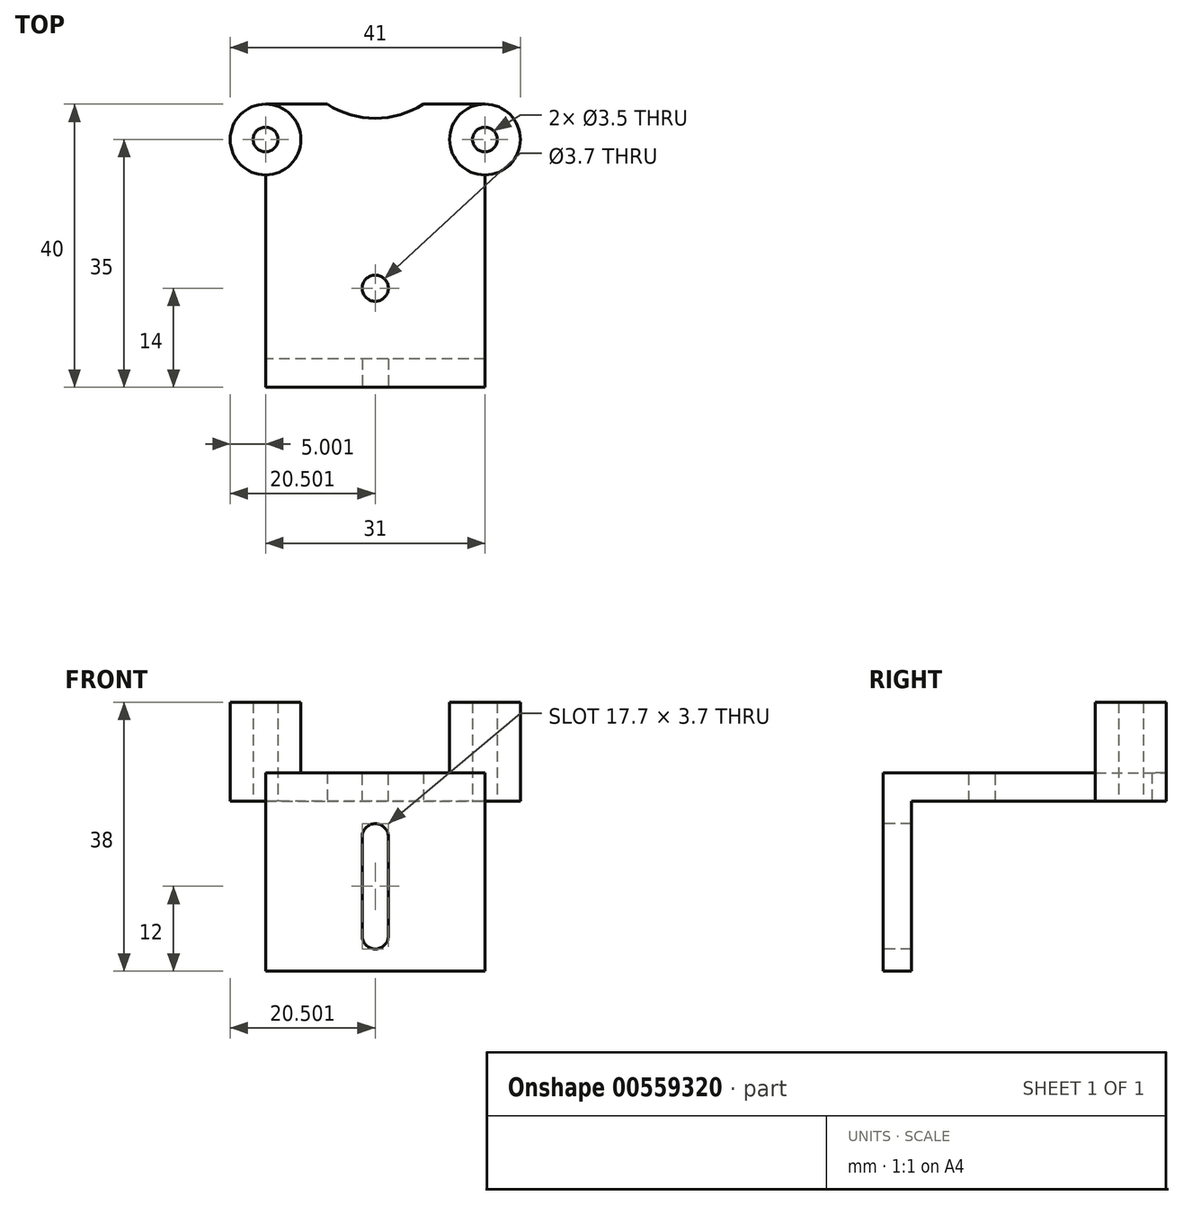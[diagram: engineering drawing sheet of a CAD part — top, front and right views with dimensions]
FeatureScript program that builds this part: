
annotation { "Feature Type Name" : "Feature", "Feature Type Description" : "" }
export const myFeature = defineFeature(function(context is Context, id is Id, definition is map)
    precondition{}
    {
        {
            var Q0;
            Q0=qCreatedBy(makeId("Top.planeOp"),FACE);
            var sketch = newSketch(context, id + "F0", { "sketchPlane" : qUnion([Q0])});
            skLineSegment(sketch, "E0", {"start": v(-4.15, -31) * mm, "end": v(26.85, -31) * mm});
            skCircle(sketch, "E1", {"center": v(26.85, -31) * mm, "radius": 1.75 * mm});
            skCircle(sketch, "E2", {"center": v(-4.15, -31) * mm, "radius": 1.75 * mm});
            skCircle(sketch, "E3", {"center": v(-4.15, -31) * mm, "radius": 5 * mm});
            skCircle(sketch, "E4", {"center": v(26.85, -31) * mm, "radius": 5 * mm});
            skLineSegment(sketch, "E5", {"start": v(-4.15, -31) * mm, "end": v(-4.15, -26) * mm, "construction": true});
            skLineSegment(sketch, "E6", {"start": v(-4.15, -26) * mm, "end": v(26.85, -26) * mm});
            skLineSegment(sketch, "E7", {"start": v(26.85, -26) * mm, "end": v(26.85, -36) * mm, "construction": true});
            skLineSegment(sketch, "E8", {"start": v(26.85, -36) * mm, "end": v(-4.15, -36) * mm});
            skLineSegment(sketch, "E9", {"start": v(-4.15, -36) * mm, "end": v(-4.15, -31) * mm, "construction": true});
            skLineSegment(sketch, "E10", {"start": v(26.85, -31) * mm, "end": v(26.85, 0) * mm});
            skLineSegment(sketch, "E11", {"start": v(26.85, 0) * mm, "end": v(-4.15, 0) * mm});
            skLineSegment(sketch, "E12", {"start": v(-4.15, 0) * mm, "end": v(-4.15, -31) * mm});
            skLineSegment(sketch, "E13", {"start": v(-4.15, -31) * mm, "end": v(26.85, 0) * mm, "construction": true});
            skLineSegment(sketch, "E14", {"start": v(-4.15, 0) * mm, "end": v(26.85, -31) * mm, "construction": true});
            skCircle(sketch, "E15", {"center": v(11.35, -15.5) * mm, "radius": 12.5 * mm});
            skSolve(sketch);
        }
        {
            var Q0;
            Q0=makeQuery(id+"F0.imprint","IMPRINT",FACE,{"disambiguationData":[TD([[makeQuery(id+"F0.imprint","IMPRINT",EDGE,{"derivedFrom":sQuery(id+"F0.wireOp",EDGE,"E2")}),-1.0]])]});
            var Q1;
            {var subQ5=sQuery(id+"F0.wireOp",EDGE,"E6");Q1=makeQuery(id+"F0.imprint","IMPRINT",FACE,{"disambiguationData":[TD([[makeQuery(id+"F0.imprint","IMPRINT",EDGE,{"derivedFrom":subQ5}),-1.0]])]});}
            var Q2;
            Q2=makeQuery(id+"F0.imprint","IMPRINT",FACE,{"disambiguationData":[TD([[makeQuery(id+"F0.imprint","IMPRINT",EDGE,{"derivedFrom":sQuery(id+"F0.wireOp",EDGE,"E1")}),-1.0]])]});
            var Q3;
            {var subQ5=sQuery(id+"F0.wireOp",EDGE,"E8");Q3=makeQuery(id+"F0.imprint","IMPRINT",FACE,{"disambiguationData":[TD([[makeQuery(id+"F0.imprint","IMPRINT",EDGE,{"derivedFrom":subQ5}),-1.0]])]});}
            var Q4;
            {var subQ1=sQuery(id+"F0.wireOp",EDGE,"E4");var subQ4=sQuery(id+"F0.wireOp",EDGE,"E0");var subQ5=makeQuery(id+"F0.imprint","INTERSECT",VERTEX,{"derivedFrom":[subQ4,subQ1]});Q4=makeQuery(id+"F0.imprint","IMPRINT",FACE,{"disambiguationData":[TD([[makeQuery(id+"F0.imprint","IMPRINT",EDGE,{"disambiguationData":[TD([[subQ5,-1.0]])],"derivedFrom":subQ4}),-1.0]])]});}
            var Q5;
            {var subQ4=sQuery(id+"F0.wireOp",EDGE,"E2");var subQ5=sQuery(id+"F0.wireOp",EDGE,"E0");var subQ6=makeQuery(id+"F0.imprint","INTERSECT",VERTEX,{"derivedFrom":[subQ5,subQ4]});Q5=makeQuery(id+"F0.imprint","IMPRINT",FACE,{"disambiguationData":[TD([[makeQuery(id+"F0.imprint","IMPRINT",EDGE,{"disambiguationData":[TD([[subQ6,-1.0]])],"derivedFrom":subQ5}),-1.0]])]});}
            extrude(context, id + "F1", {"entities" : qUnion([Q0, Q1, Q2, Q3, Q4, Q5]), "depth" : 4 * mm, "offsetDistance" : 25 * mm});
        }
        {
            var Q0;
            Q0=makeQuery(id+"F0.imprint","IMPRINT",FACE,{"disambiguationData":[TD([[makeQuery(id+"F0.imprint","IMPRINT",EDGE,{"derivedFrom":sQuery(id+"F0.wireOp",EDGE,"E2")}),-1.0]])]});
            var Q1;
            Q1=makeQuery(id+"F0.imprint","IMPRINT",FACE,{"disambiguationData":[TD([[makeQuery(id+"F0.imprint","IMPRINT",EDGE,{"derivedFrom":sQuery(id+"F0.wireOp",EDGE,"E1")}),-1.0]])]});
            var Q2;
            {var subQ4=sQuery(id+"F0.wireOp",EDGE,"E2");var subQ5=sQuery(id+"F0.wireOp",EDGE,"E0");var subQ6=makeQuery(id+"F0.imprint","INTERSECT",VERTEX,{"derivedFrom":[subQ5,subQ4]});Q2=makeQuery(id+"F0.imprint","IMPRINT",FACE,{"disambiguationData":[TD([[makeQuery(id+"F0.imprint","IMPRINT",EDGE,{"disambiguationData":[TD([[subQ6,-1.0]])],"derivedFrom":subQ5}),-1.0]])]});}
            var Q3;
            {var subQ1=sQuery(id+"F0.wireOp",EDGE,"E4");var subQ4=sQuery(id+"F0.wireOp",EDGE,"E0");var subQ5=makeQuery(id+"F0.imprint","INTERSECT",VERTEX,{"derivedFrom":[subQ4,subQ1]});Q3=makeQuery(id+"F0.imprint","IMPRINT",FACE,{"disambiguationData":[TD([[makeQuery(id+"F0.imprint","IMPRINT",EDGE,{"disambiguationData":[TD([[subQ5,-1.0]])],"derivedFrom":subQ4}),-1.0]])]});}
            extrude(context, id + "F2", {"entities" : qUnion([Q0, Q1, Q2, Q3]), "operationType" : NewBodyOperationType.ADD, "depth" : 14 * mm, "offsetDistance" : 25 * mm});
        }
        {
            var Q0;
            Q0=makeQuery(id+"F1.opExtrude","SWEPT_FACE",FACE,{"disambiguationData":[OSD([sQuery(id+"F0.wireOp",EDGE,"E8")])]});
            extrude(context, id + "F3", {"entities" : qUnion([Q0]), "operationType" : NewBodyOperationType.ADD, "depth" : 30 * mm, "offsetDistance" : 25 * mm});
        }
        {
            var Q0;
            {var subQ0=sQuery(id+"F0.wireOp",EDGE,"E8");Q0=makeQuery(id+"F3.boolean.opBoolean","MERGE",FACE,{"derivedFrom":[makeQuery(id+"F1.opExtrude","CAP_FACE",FACE,{"disambiguationData":[OSD([sQuery(id+"F0.wireOp",EDGE,"E1"),sQuery(id+"F0.wireOp",EDGE,"E2"),sQuery(id+"F0.wireOp",EDGE,"E3"),sQuery(id+"F0.wireOp",EDGE,"E4"),sQuery(id+"F0.wireOp",EDGE,"E6"),subQ0])],"isStart":true}),makeQuery(id+"F3.opExtrude","SWEPT_FACE",FACE,{"disambiguationData":[OSD([subQ0]),TDD([makeQuery(id+"F1.opExtrude","CAP_EDGE",EDGE,{"disambiguationData":[OSD([subQ0])],"isStart":true})])]})]});}
            var sketch = newSketch(context, id + "F4", { "sketchPlane" : qUnion([Q0])});
            skLineSegment(sketch, "E16", {"start": v(-4.15, 66) * mm, "end": v(26.85, 66) * mm});
            skLineSegment(sketch, "E17", {"start": v(26.85, 66) * mm, "end": v(26.85, 62) * mm});
            skLineSegment(sketch, "E18", {"start": v(26.85, 62) * mm, "end": v(-4.15, 62) * mm});
            skLineSegment(sketch, "E19", {"start": v(-4.15, 62) * mm, "end": v(-4.15, 66) * mm});
            skSolve(sketch);
        }
        {
            var Q0;
            Q0=makeQuery(id+"F4.imprint","IMPRINT",FACE,{"disambiguationData":[TD([[makeQuery(id+"F4.imprint","IMPRINT",EDGE,{"derivedFrom":sQuery(id+"F4.wireOp",EDGE,"E16")}),1.0]])]});
            extrude(context, id + "F5", {"entities" : qUnion([Q0]), "operationType" : NewBodyOperationType.ADD, "depth" : 24 * mm, "offsetDistance" : 25 * mm});
        }
        {
            var Q0;
            Q0=makeQuery(id+"F5.boolean.opBoolean","MERGE",FACE,{"derivedFrom":[makeQuery(id+"F3.opExtrude","CAP_FACE",FACE,{"disambiguationData":[OSD([sQuery(id+"F0.wireOp",EDGE,"E8")])],"isStart":false}),makeQuery(id+"F5.opExtrude","SWEPT_FACE",FACE,{"disambiguationData":[OSD([sQuery(id+"F4.wireOp",EDGE,"E16")])]})]});
            var sketch = newSketch(context, id + "F6", { "sketchPlane" : qUnion([Q0])});
            skLineSegment(sketch, "E20", {"start": v(-4.15, 4) * mm, "end": v(26.85, 4) * mm, "construction": true});
            skLineSegment(sketch, "E21", {"start": v(26.85, 4) * mm, "end": v(26.85, 0) * mm, "construction": true});
            skLineSegment(sketch, "E22", {"start": v(26.85, 0) * mm, "end": v(-4.15, 0) * mm, "construction": true});
            skLineSegment(sketch, "E23", {"start": v(-4.15, 0) * mm, "end": v(-4.15, 4) * mm, "construction": true});
            skLineSegment(sketch, "E24", {"start": v(-4.15, 0) * mm, "end": v(26.85, -24) * mm, "construction": true});
            skLineSegment(sketch, "E25", {"start": v(26.85, 0) * mm, "end": v(-4.15, -24) * mm, "construction": true});
            skLineSegment(sketch, "E26", {"start": v(13.2, -12) * mm, "end": v(13.2, -5) * mm});
            skLineSegment(sketch, "E27", {"start": v(9.5, -12) * mm, "end": v(9.5, -5) * mm});
            skArc(sketch, "E28", {"start": v(13.2, -5) * mm, "mid": v(11.35, -3.15) * mm, "end": v(9.5, -5) * mm});
            skArc(sketch, "E29.MirrorCS", {"start": v(13.2, -19) * mm, "mid": v(11.35, -20.85) * mm, "end": v(9.5, -19) * mm});
            skLineSegment(sketch, "E30.MirrorCS", {"start": v(13.2, -12) * mm, "end": v(13.2, -19) * mm});
            skLineSegment(sketch, "E31.MirrorCS", {"start": v(9.5, -12) * mm, "end": v(9.5, -19) * mm});
            skSolve(sketch);
        }
        {
            var Q0;
            {var subQ0=sQuery(id+"F0.wireOp",EDGE,"E8");Q0=makeQuery(id+"F3.boolean.opBoolean","MERGE",FACE,{"derivedFrom":[makeQuery(id+"F1.opExtrude","CAP_FACE",FACE,{"disambiguationData":[OSD([sQuery(id+"F0.wireOp",EDGE,"E1"),sQuery(id+"F0.wireOp",EDGE,"E2"),sQuery(id+"F0.wireOp",EDGE,"E3"),sQuery(id+"F0.wireOp",EDGE,"E4"),sQuery(id+"F0.wireOp",EDGE,"E6"),subQ0])],"isStart":false}),makeQuery(id+"F3.opExtrude","SWEPT_FACE",FACE,{"disambiguationData":[OSD([subQ0]),TDD([makeQuery(id+"F1.opExtrude","CAP_EDGE",EDGE,{"disambiguationData":[OSD([subQ0])],"isStart":false})])]})]});}
            var sketch = newSketch(context, id + "F7", { "sketchPlane" : qUnion([Q0])});
            skLineSegment(sketch, "E32", {"start": v(26.85, -66) * mm, "end": v(-4.15, -66) * mm, "construction": true});
            skLineSegment(sketch, "E33", {"start": v(-4.15, -66) * mm, "end": v(-4.15, -62) * mm, "construction": true});
            skLineSegment(sketch, "E34", {"start": v(-4.15, -62) * mm, "end": v(26.85, -62) * mm, "construction": true});
            skLineSegment(sketch, "E35", {"start": v(26.85, -62) * mm, "end": v(26.85, -66) * mm, "construction": true});
            skLineSegment(sketch, "E36", {"start": v(-4.15, -62) * mm, "end": v(-4.15, -42) * mm, "construction": true});
            skLineSegment(sketch, "E37", {"start": v(-4.15, -42) * mm, "end": v(26.85, -42) * mm, "construction": true});
            skLineSegment(sketch, "E38", {"start": v(26.85, -42) * mm, "end": v(26.85, -62) * mm, "construction": true});
            skLineSegment(sketch, "E39", {"start": v(-4.15, -42) * mm, "end": v(26.85, -62) * mm, "construction": true});
            skLineSegment(sketch, "E40", {"start": v(26.85, -42) * mm, "end": v(-4.15, -62) * mm, "construction": true});
            skCircle(sketch, "E41", {"center": v(11.35, -52) * mm, "radius": 1.85 * mm});
            skSolve(sketch);
        }
        {
            var Q0;
            Q0=makeQuery(id+"F6.imprint","IMPRINT",FACE,{"disambiguationData":[TD([[makeQuery(id+"F6.imprint","IMPRINT",EDGE,{"derivedFrom":sQuery(id+"F6.wireOp",EDGE,"E26")}),1.0]])]});
            extrude(context, id + "F8", {"entities" : qUnion([Q0]), "operationType" : NewBodyOperationType.REMOVE, "oppositeDirection" : true, "depth" : 25 * mm, "offsetDistance" : 25 * mm});
        }
        {
            var Q0;
            Q0=makeQuery(id+"F7.imprint","IMPRINT",FACE,{"disambiguationData":[TD([[makeQuery(id+"F7.imprint","IMPRINT",EDGE,{"derivedFrom":sQuery(id+"F7.wireOp",EDGE,"E41")}),1.0]])]});
            var Q1;
            Q1=sQuery(id+"F7.wireOp",EDGE,"E41");
            extrude(context, id + "F9", {"entities" : qUnion([Q0]), "operationType" : NewBodyOperationType.REMOVE, "surfaceEntities" : qUnion([Q1]), "oppositeDirection" : true, "depth" : 25 * mm, "offsetDistance" : 25 * mm});
        }
    });
